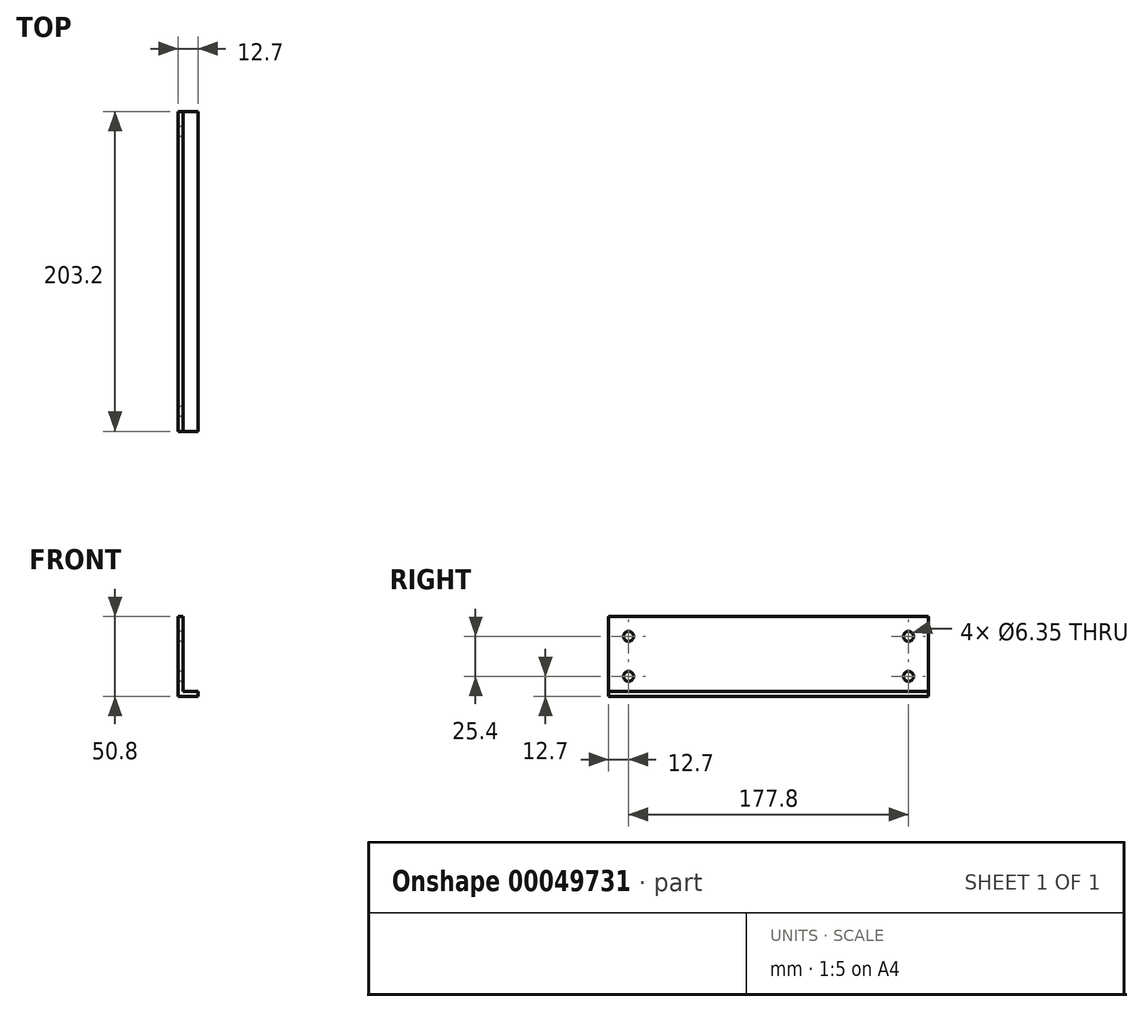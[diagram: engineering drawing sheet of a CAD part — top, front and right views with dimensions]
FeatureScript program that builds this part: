
annotation { "Feature Type Name" : "Feature", "Feature Type Description" : "" }
export const myFeature = defineFeature(function(context is Context, id is Id, definition is map)
    precondition{}
    {
        {
            var Q0;
            Q0=qCreatedBy(makeId("Front.planeOp"),FACE);
            var sketch = newSketch(context, id + "F0", { "sketchPlane" : qUnion([Q0])});
            skLineSegment(sketch, "E0", {"start": v(-12.7, 50.8) * mm, "end": v(-12.7, 0) * mm});
            skLineSegment(sketch, "E1", {"start": v(-12.7, 0) * mm, "end": v(0, 0) * mm});
            skLineSegment(sketch, "E2", {"start": v(0, 0) * mm, "end": v(0, 3.18) * mm});
            skLineSegment(sketch, "E3", {"start": v(-9.52, 3.17) * mm, "end": v(-9.52, 50.8) * mm});
            skLineSegment(sketch, "E4", {"start": v(-9.52, 50.8) * mm, "end": v(-12.7, 50.8) * mm});
            skLineSegment(sketch, "E5", {"start": v(0, 3.18) * mm, "end": v(-9.52, 3.17) * mm});
            skSolve(sketch);
        }
        {
            var Q0;
            Q0 = qSketchRegion(id + "F0", true);
            extrude(context, id + "F1", {"entities" : qUnion([Q0]), "depth" : 101.6 * mm});
        }
        {
            var Q0;
            Q0=makeQuery(id+"F1.opExtrude","SWEPT_FACE",FACE,{"disambiguationData":[OSD([sQuery(id+"F0.wireOp",EDGE,"E0")])]});
            var sketch = newSketch(context, id + "F2", { "sketchPlane" : qUnion([Q0])});
            skPoint(sketch, "E6", {"position": v(88.9, 38.1) * mm});
            skPoint(sketch, "E7", {"position": v(88.9, 12.7) * mm});
            skSolve(sketch);
        }
        {
            var Q0;
            Q0=sQuery(id+"F2.wireOp",VERTEX,"E6");
            var Q1;
            Q1=sQuery(id+"F2.wireOp",VERTEX,"E7");
            var Q2;
            Q2=makeQuery(id+"F1.opExtrude","SWEPT_BODY",BODY,{"disambiguationData":[OSD([sQuery(id+"F0.wireOp",EDGE,"E0"),sQuery(id+"F0.wireOp",EDGE,"E1"),sQuery(id+"F0.wireOp",EDGE,"E2"),sQuery(id+"F0.wireOp",EDGE,"E3"),sQuery(id+"F0.wireOp",EDGE,"E4"),sQuery(id+"F0.wireOp",EDGE,"E5")])]});
            hole(context, id + "F3", {"style" : HoleStyle.SIMPLE, "holeDiameter" : 6.35 * mm, "endStyle" : HoleEndStyle.THROUGH, "locations" : qUnion([Q0, Q1]), "scope" : qUnion([Q2])});
        }
        {
            var Q0;
            Q0=makeQuery(id+"F1.opExtrude","SWEPT_BODY",BODY,{"disambiguationData":[OSD([sQuery(id+"F0.wireOp",EDGE,"E0"),sQuery(id+"F0.wireOp",EDGE,"E1"),sQuery(id+"F0.wireOp",EDGE,"E2"),sQuery(id+"F0.wireOp",EDGE,"E3"),sQuery(id+"F0.wireOp",EDGE,"E4"),sQuery(id+"F0.wireOp",EDGE,"E5")])]});
            var Q1;
            Q1=qCreatedBy(makeId("Front.planeOp"),FACE);
            mirror(context, id + "F4", {"operationType" : NewBodyOperationType.ADD, "entities" : qUnion([Q0]), "mirrorPlane" : qUnion([Q1])});
        }
    });
